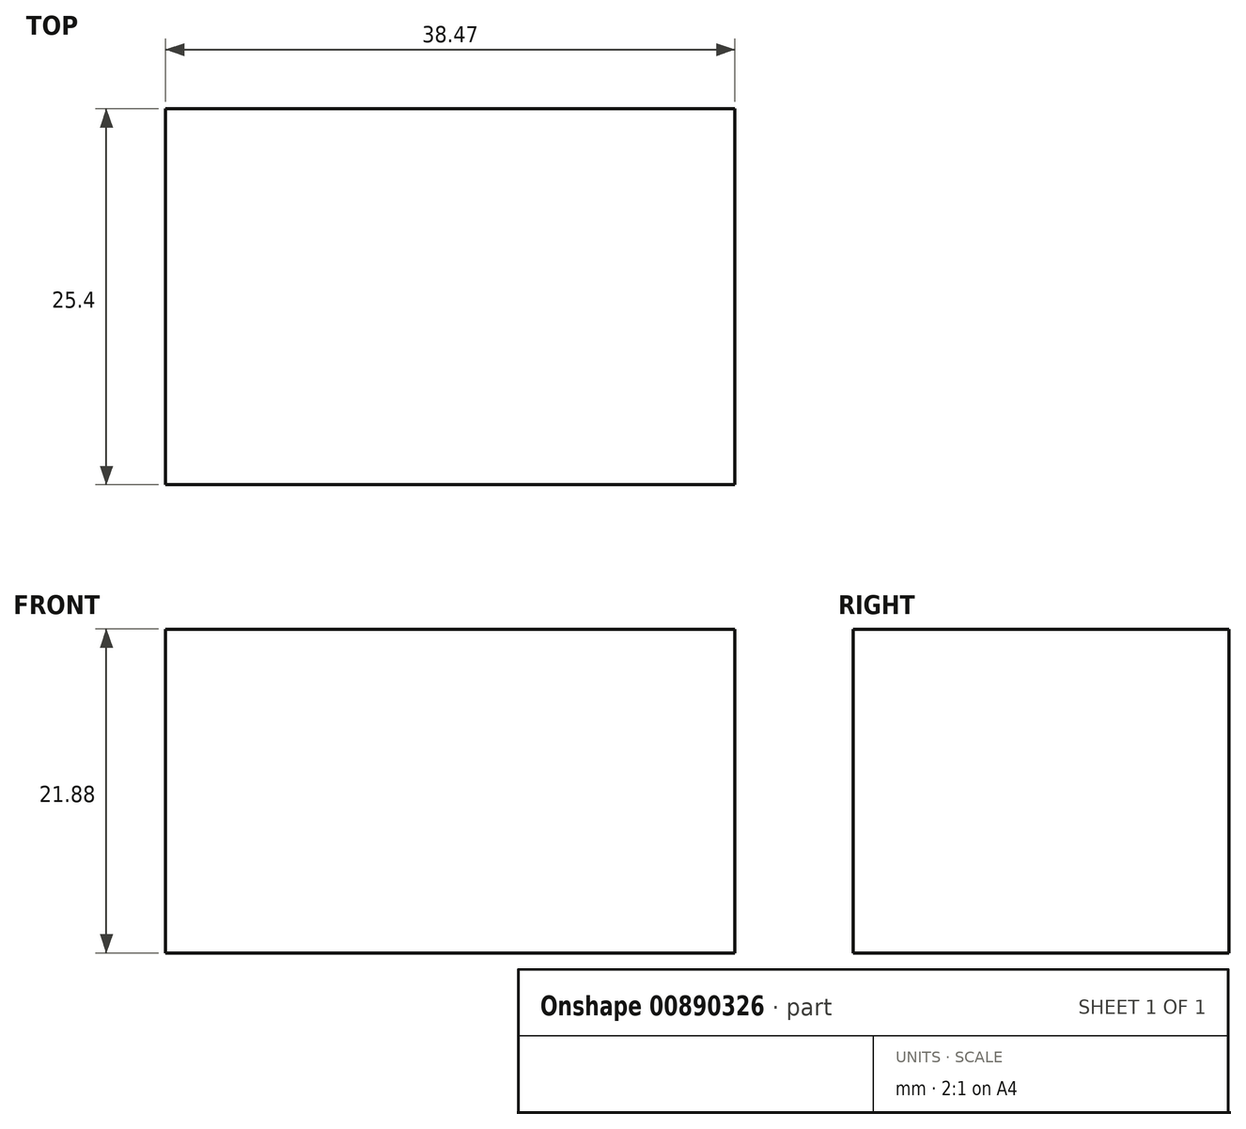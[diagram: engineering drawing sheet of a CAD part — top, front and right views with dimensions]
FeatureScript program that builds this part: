
annotation { "Feature Type Name" : "Feature", "Feature Type Description" : "" }
export const myFeature = defineFeature(function(context is Context, id is Id, definition is map)
    precondition{}
    {
        {
            var Q0;
            Q0=qCreatedBy(makeId("Front.planeOp"),FACE);
            var sketch = newSketch(context, id + "F0", { "sketchPlane" : qUnion([Q0])});
            skLineSegment(sketch, "E0.bottom", {"start": v(-18.81, 0) * mm, "end": v(19.66, 0) * mm});
            skLineSegment(sketch, "E0.top", {"start": v(-18.81, 21.88) * mm, "end": v(19.66, 21.88) * mm});
            skLineSegment(sketch, "E0.left", {"start": v(-18.81, 0) * mm, "end": v(-18.81, 21.88) * mm});
            skLineSegment(sketch, "E0.right", {"start": v(19.66, 0) * mm, "end": v(19.66, 21.88) * mm});
            skSolve(sketch);
        }
        {
            var Q0;
            Q0 = qSketchRegion(id + "F0", true);
            extrude(context, id + "F1", {"entities" : qUnion([Q0]), "depth" : 25.4 * mm, "offsetDistance" : 25.4 * mm});
        }
    });
